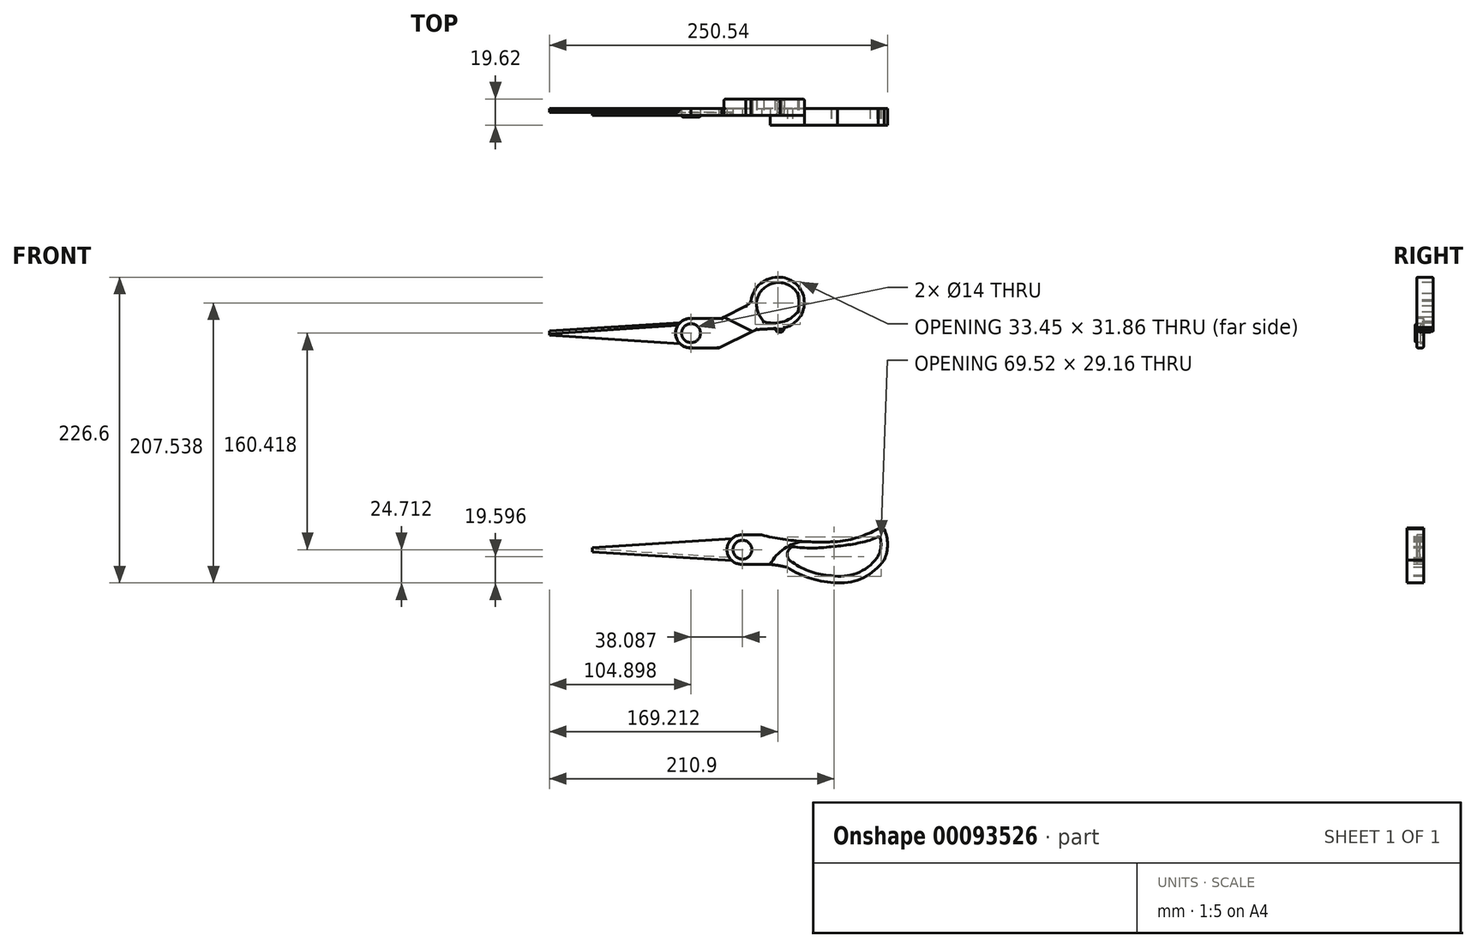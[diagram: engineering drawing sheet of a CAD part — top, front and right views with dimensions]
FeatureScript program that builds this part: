
annotation { "Feature Type Name" : "Feature", "Feature Type Description" : "" }
export const myFeature = defineFeature(function(context is Context, id is Id, definition is map)
    precondition{}
    {
        {
            var Q0;
            Q0=qCreatedBy(makeId("Front.planeOp"),FACE);
            var sketch = newSketch(context, id + "F0", { "sketchPlane" : qUnion([Q0])});
            skLineSegment(sketch, "E0", {"start": v(-93.78, 0) * mm, "end": v(95.08, 0) * mm, "construction": true});
            skLineSegment(sketch, "E1", {"start": v(-93.78, 0) * mm, "end": v(5.93, 0) * mm, "construction": true});
            skLineSegment(sketch, "E2", {"start": v(-93.78, 0) * mm, "end": v(-93.78, -1.57) * mm, "construction": true});
            skLineSegment(sketch, "E3", {"start": v(-93.78, 0) * mm, "end": v(-93.78, 1.57) * mm, "construction": true});
            skLineSegment(sketch, "E4", {"start": v(5.93, 0) * mm, "end": v(5.93, 8.05) * mm, "construction": true});
            skLineSegment(sketch, "E5", {"start": v(5.93, 0) * mm, "end": v(5.93, -8.05) * mm, "construction": true});
            skLineSegment(sketch, "E6", {"start": v(-93.78, 1.57) * mm, "end": v(5.93, 8.05) * mm});
            skLineSegment(sketch, "E7", {"start": v(-93.78, -1.57) * mm, "end": v(5.93, -8.05) * mm});
            skLineSegment(sketch, "E8", {"start": v(-93.78, 1.57) * mm, "end": v(-93.78, -1.57) * mm});
            skLineSegment(sketch, "E9", {"start": v(95.08, 0) * mm, "end": v(95.08, 32) * mm, "construction": true});
            skLineSegment(sketch, "E10", {"start": v(5.93, 0) * mm, "end": v(31.53, 0) * mm, "construction": true});
            skLineSegment(sketch, "E11", {"start": v(31.53, 0) * mm, "end": v(31.53, -10.87) * mm, "construction": true});
            skLineSegment(sketch, "E12", {"start": v(5.93, 0) * mm, "end": v(33.93, 0) * mm, "construction": true});
            skLineSegment(sketch, "E13", {"start": v(33.93, 0) * mm, "end": v(33.93, 10.87) * mm, "construction": true});
            skLineSegment(sketch, "E14", {"start": v(31.53, 0) * mm, "end": v(11.12, 0) * mm, "construction": true});
            skLineSegment(sketch, "E15", {"start": v(11.12, 0) * mm, "end": v(11.12, 10.87) * mm, "construction": true});
            skLineSegment(sketch, "E16", {"start": v(11.12, 0) * mm, "end": v(11.12, -10.87) * mm, "construction": true});
            skLineSegment(sketch, "E17", {"start": v(11.12, 0) * mm, "end": v(-0.31, 0) * mm, "construction": true});
            skArc(sketch, "E18", {"start": v(11.12, 10.87) * mm, "mid": v(-0.31, 0) * mm, "end": v(11.12, -10.87) * mm});
            skLineSegment(sketch, "E19", {"start": v(11.12, 10.87) * mm, "end": v(33.93, 10.87) * mm, "construction": true});
            skLineSegment(sketch, "E20", {"start": v(11.12, -10.87) * mm, "end": v(31.53, -10.87) * mm, "construction": true});
            skLineSegment(sketch, "E21", {"start": v(33.93, 0) * mm, "end": v(95.08, 32) * mm, "construction": true});
            skLineSegment(sketch, "E22", {"start": v(95.08, 32) * mm, "end": v(95.08, 50.8) * mm, "construction": true});
            skLineSegment(sketch, "E23", {"start": v(95.08, 32) * mm, "end": v(95.08, 13.2) * mm, "construction": true});
            skLineSegment(sketch, "E24", {"start": v(95.08, 32.55) * mm, "end": v(90.03, 29.91) * mm, "construction": true});
            skLineSegment(sketch, "E25", {"start": v(90.03, 29.36) * mm, "end": v(64.24, 15.86) * mm, "construction": true});
            skLineSegment(sketch, "E26", {"start": v(90.03, 29.91) * mm, "end": v(77.13, 23.16) * mm, "construction": true});
            skLineSegment(sketch, "E27", {"start": v(77.13, 22.6) * mm, "end": v(77.13, 3.81) * mm, "construction": true});
            skLineSegment(sketch, "E28", {"start": v(77.13, 22.6) * mm, "end": v(77.13, 41.41) * mm, "construction": true});
            skArc(sketch, "E29", {"start": v(77.13, 3.81) * mm, "mid": v(95.09, 22.61) * mm, "end": v(77.13, 41.41) * mm});
            skLineSegment(sketch, "E30", {"start": v(33.93, 0) * mm, "end": v(59.92, 13.6) * mm, "construction": true});
            skLineSegment(sketch, "E31", {"start": v(59.92, 13.6) * mm, "end": v(59.92, 24.47) * mm, "construction": true});
            skLineSegment(sketch, "E32", {"start": v(59.92, 13.6) * mm, "end": v(59.92, 2.73) * mm, "construction": true});
            skLineSegment(sketch, "E33", {"start": v(33.93, 10.87) * mm, "end": v(59.92, 24.47) * mm, "construction": true});
            skArc(sketch, "E34", {"start": v(77.13, 41.41) * mm, "mid": v(62.77, 36.88) * mm, "end": v(55.42, 23.74) * mm});
            skArc(sketch, "E35", {"start": v(51.68, 20.16) * mm, "mid": v(53.85, 21.63) * mm, "end": v(55.42, 23.74) * mm});
            skLineSegment(sketch, "E36", {"start": v(31.53, -10.87) * mm, "end": v(59.92, 2.73) * mm, "construction": true});
            skArc(sketch, "E37", {"start": v(59.92, 2.73) * mm, "mid": v(68.53, 3.17) * mm, "end": v(77.13, 3.81) * mm});
            skCircle(sketch, "E38", {"center": v(11.12, 0) * mm, "radius": 7 * mm});
            skLineSegment(sketch, "E39", {"start": v(95.08, 0.99) * mm, "end": v(73.17, 0.99) * mm, "construction": true});
            skLineSegment(sketch, "E40", {"start": v(73.17, 3.5) * mm, "end": v(73.17, 0.86) * mm});
            skLineSegment(sketch, "E41", {"start": v(73.17, 0.86) * mm, "end": v(80.38, 0.86) * mm});
            skLineSegment(sketch, "E42", {"start": v(80.38, 0.86) * mm, "end": v(80.38, 4.25) * mm});
            skLineSegment(sketch, "E43", {"start": v(77.5, 3.83) * mm, "end": v(77.5, 9.53) * mm, "construction": true});
            skLineSegment(sketch, "E44", {"start": v(95.08, 21.98) * mm, "end": v(86.61, 21.98) * mm, "construction": true});
            skLineSegment(sketch, "E45", {"start": v(65.06, 2.97) * mm, "end": v(65.06, 8.67) * mm});
            skLineSegment(sketch, "E46", {"start": v(90.15, 9.9) * mm, "end": v(90.15, 15.6) * mm, "construction": true});
            skArc(sketch, "E47", {"start": v(90.03, 29.36) * mm, "mid": v(73.3, 37.3) * mm, "end": v(59.92, 24.47) * mm});
            skArc(sketch, "E48", {"start": v(90.15, 15.6) * mm, "mid": v(91.16, 22.49) * mm, "end": v(90.03, 29.36) * mm});
            skArc(sketch, "E49", {"start": v(59.92, 24.47) * mm, "mid": v(60.59, 15.95) * mm, "end": v(65.06, 8.67) * mm});
            skArc(sketch, "E50", {"start": v(65.06, 8.67) * mm, "mid": v(78.66, 8.31) * mm, "end": v(90.15, 15.6) * mm});
            skLineSegment(sketch, "E51", {"start": v(11.12, 10.87) * mm, "end": v(33.93, 10.87) * mm});
            skLineSegment(sketch, "E52", {"start": v(33.93, 10.87) * mm, "end": v(51.68, 20.16) * mm});
            skLineSegment(sketch, "E53", {"start": v(11.12, -10.87) * mm, "end": v(31.53, -10.87) * mm});
            skLineSegment(sketch, "E54", {"start": v(31.53, -10.87) * mm, "end": v(59.92, 2.73) * mm});
            skLineSegment(sketch, "E55", {"start": v(31.53, -10.87) * mm, "end": v(54.22, 0) * mm, "construction": true});
            skLineSegment(sketch, "E56", {"start": v(31.53, -10.87) * mm, "end": v(50.38, -1.84) * mm, "construction": true});
            skLineSegment(sketch, "E57", {"start": v(56.83, 1.25) * mm, "end": v(35.63, 11.76) * mm});
            skSolve(sketch);
        }
        {
            var Q0;
            {var subQ0=sQuery(id+"F0.wireOp",EDGE,"E8");Q0=makeQuery(id+"F0.imprint","IMPRINT",FACE,{"disambiguationData":[TD([[makeQuery(id+"F0.imprint","IMPRINT",EDGE,{"derivedFrom":subQ0}),1.0]])]});}
            extrude(context, id + "F1", {"entities" : qUnion([Q0]), "oppositeDirection" : true, "depth" : 5.1 * mm, "hasSecondDirection" : true, "secondDirectionOppositeDirection" : true, "secondDirectionDepth" : 2.53 * mm});
        }
        {
            var Q0;
            Q0=makeQuery(id+"F0.imprint","IMPRINT",FACE,{"disambiguationData":[TD([[makeQuery(id+"F0.imprint","IMPRINT",EDGE,{"derivedFrom":sQuery(id+"F0.wireOp",EDGE,"E38")}),-1.0]])]});
            extrude(context, id + "F2", {"entities" : qUnion([Q0]), "oppositeDirection" : true, "depth" : 5.1 * mm});
        }
        {
            var Q0;
            {var subQ9=sQuery(id+"F0.wireOp",EDGE,"E34");Q0=makeQuery(id+"F0.imprint","IMPRINT",FACE,{"disambiguationData":[TD([[makeQuery(id+"F0.imprint","IMPRINT",EDGE,{"derivedFrom":subQ9}),1.0]])]});}
            var Q1;
            {var subQ0=sQuery(id+"F0.wireOp",EDGE,"E40");Q1=makeQuery(id+"F0.imprint","IMPRINT",FACE,{"disambiguationData":[TD([[makeQuery(id+"F0.imprint","IMPRINT",EDGE,{"derivedFrom":subQ0}),1.0]])]});}
            extrude(context, id + "F3", {"entities" : qUnion([Q0, Q1]), "oppositeDirection" : true, "depth" : 12.33 * mm});
        }
        {
            var Q0;
            Q0=makeQuery(id+"F3.opExtrude","CAP_EDGE",EDGE,{"disambiguationData":[OSD([sQuery(id+"F0.wireOp",EDGE,"E29")])],"isStart":false});
            var Q1;
            Q1=makeQuery(id+"F3.opExtrude","CAP_EDGE",EDGE,{"disambiguationData":[OSD([sQuery(id+"F0.wireOp",EDGE,"E34")])],"isStart":false});
            var Q2;
            Q2=makeQuery(id+"F3.opExtrude","CAP_EDGE",EDGE,{"disambiguationData":[OSD([sQuery(id+"F0.wireOp",EDGE,"E35")])],"isStart":false});
            var Q3;
            Q3=makeQuery(id+"F3.opExtrude","CAP_EDGE",EDGE,{"disambiguationData":[OSD([sQuery(id+"F0.wireOp",EDGE,"E52")])],"isStart":false});
            var Q4;
            Q4=makeQuery(id+"F3.opExtrude","CAP_EDGE",EDGE,{"disambiguationData":[OSD([sQuery(id+"F0.wireOp",EDGE,"E37")])],"isStart":false});
            var Q5;
            Q5=makeQuery(id+"F3.opExtrude","CAP_EDGE",EDGE,{"disambiguationData":[OSD([sQuery(id+"F0.wireOp",EDGE,"E54")])],"isStart":false});
            var Q6;
            Q6=makeQuery(id+"F3.opExtrude","CAP_EDGE",EDGE,{"disambiguationData":[OSD([sQuery(id+"F0.wireOp",EDGE,"E34")])],"isStart":true});
            var Q7;
            Q7=makeQuery(id+"F3.opExtrude","CAP_EDGE",EDGE,{"disambiguationData":[OSD([sQuery(id+"F0.wireOp",EDGE,"E35")])],"isStart":true});
            var Q8;
            {var subQ0=sQuery(id+"F0.wireOp",EDGE,"E52");Q8=makeQuery(id+"F3.boolean.opBoolean","MERGE",EDGE,{"derivedFrom":[makeQuery(id+"F2.opExtrude","CAP_EDGE",EDGE,{"disambiguationData":[OSD([subQ0])],"isStart":true}),makeQuery(id+"F3.opExtrude","CAP_EDGE",EDGE,{"disambiguationData":[OSD([subQ0])],"isStart":true})]});}
            var Q9;
            Q9=makeQuery(id+"F3.opExtrude","CAP_EDGE",EDGE,{"disambiguationData":[OSD([sQuery(id+"F0.wireOp",EDGE,"E29")])],"isStart":true});
            var Q10;
            Q10=makeQuery(id+"F3.opExtrude","CAP_EDGE",EDGE,{"disambiguationData":[OSD([sQuery(id+"F0.wireOp",EDGE,"E37")])],"isStart":true});
            var Q11;
            {var subQ0=sQuery(id+"F0.wireOp",EDGE,"E54");Q11=makeQuery(id+"F3.boolean.opBoolean","MERGE",EDGE,{"derivedFrom":[makeQuery(id+"F2.opExtrude","CAP_EDGE",EDGE,{"disambiguationData":[OSD([subQ0])],"isStart":true}),makeQuery(id+"F3.opExtrude","CAP_EDGE",EDGE,{"disambiguationData":[OSD([subQ0])],"isStart":true})]});}
            var Q12;
            Q12=makeQuery(id+"F2.opExtrude","CAP_EDGE",EDGE,{"disambiguationData":[OSD([sQuery(id+"F0.wireOp",EDGE,"E53")])],"isStart":true});
            var Q13;
            Q13=makeQuery(id+"F2.opExtrude","CAP_EDGE",EDGE,{"disambiguationData":[OSD([sQuery(id+"F0.wireOp",EDGE,"E18")])],"isStart":true});
            var Q14;
            Q14=makeQuery(id+"F2.opExtrude","CAP_EDGE",EDGE,{"disambiguationData":[OSD([sQuery(id+"F0.wireOp",EDGE,"E51")])],"isStart":true});
            var Q15;
            Q15=makeQuery(id+"F2.opExtrude","CAP_EDGE",EDGE,{"disambiguationData":[OSD([sQuery(id+"F0.wireOp",EDGE,"E51")])],"isStart":false});
            var Q16;
            Q16=makeQuery(id+"F2.opExtrude","CAP_EDGE",EDGE,{"disambiguationData":[OSD([sQuery(id+"F0.wireOp",EDGE,"E18")])],"isStart":false});
            var Q17;
            Q17=makeQuery(id+"F2.opExtrude","CAP_EDGE",EDGE,{"disambiguationData":[OSD([sQuery(id+"F0.wireOp",EDGE,"E53")])],"isStart":false});
            var Q18;
            Q18=makeQuery(id+"F2.opExtrude","CAP_EDGE",EDGE,{"disambiguationData":[OSD([sQuery(id+"F0.wireOp",EDGE,"E54")])],"isStart":false});
            var Q19;
            Q19=makeQuery(id+"F2.opExtrude","CAP_EDGE",EDGE,{"disambiguationData":[OSD([sQuery(id+"F0.wireOp",EDGE,"E52")])],"isStart":false});
            fillet(context, id + "F4", {"entities" : qUnion([Q0, Q1, Q2, Q3, Q4, Q5, Q6, Q7, Q8, Q9, Q10, Q11, Q12, Q13, Q14, Q15, Q16, Q17, Q18, Q19]), "radius" : 1 * mm, "tangentPropagation" : true, "allowEdgeOverflow" : false});
        }
        {
            var Q0;
            Q0=makeQuery(id+"F3.opExtrude","CAP_EDGE",EDGE,{"disambiguationData":[OSD([sQuery(id+"F0.wireOp",EDGE,"E50")])],"isStart":false});
            var Q1;
            Q1=makeQuery(id+"F3.opExtrude","CAP_EDGE",EDGE,{"disambiguationData":[OSD([sQuery(id+"F0.wireOp",EDGE,"E48")])],"isStart":false});
            var Q2;
            Q2=makeQuery(id+"F3.opExtrude","CAP_EDGE",EDGE,{"disambiguationData":[OSD([sQuery(id+"F0.wireOp",EDGE,"E47")])],"isStart":false});
            var Q3;
            Q3=makeQuery(id+"F3.opExtrude","CAP_EDGE",EDGE,{"disambiguationData":[OSD([sQuery(id+"F0.wireOp",EDGE,"E49")])],"isStart":false});
            fillet(context, id + "F5", {"entities" : qUnion([Q0, Q1, Q2, Q3]), "radius" : 1 * mm, "tangentPropagation" : true, "allowEdgeOverflow" : false});
        }
        {
            var Q0;
            Q0=makeQuery(id+"F3.opExtrude","CAP_EDGE",EDGE,{"disambiguationData":[OSD([sQuery(id+"F0.wireOp",EDGE,"E41")])],"isStart":false});
            var Q1;
            Q1=makeQuery(id+"F3.opExtrude","CAP_EDGE",EDGE,{"disambiguationData":[OSD([sQuery(id+"F0.wireOp",EDGE,"E41")])],"isStart":true});
            chamfer(context, id + "F6", {"entities" : qUnion([Q0, Q1]), "width" : 2 * mm, "tangentPropagation" : true});
        }
        {
            var Q0;
            Q0=makeQuery(id+"F3.opExtrude","SWEPT_EDGE",EDGE,{"disambiguationData":[OSD([sQuery(id+"F0.wireOp",EDGE,"E41"),sQuery(id+"F0.wireOp",EDGE,"E42")])]});
            var Q1;
            Q1=makeQuery(id+"F3.opExtrude","SWEPT_EDGE",EDGE,{"disambiguationData":[OSD([sQuery(id+"F0.wireOp",EDGE,"E40"),sQuery(id+"F0.wireOp",EDGE,"E41")])]});
            chamfer(context, id + "F7", {"entities" : qUnion([Q0, Q1]), "width" : 2 * mm, "tangentPropagation" : true});
        }
        {
            var Q0;
            Q0=qCreatedBy(makeId("Front.planeOp"),FACE);
            var sketch = newSketch(context, id + "F8", { "sketchPlane" : qUnion([Q0])});
            skLineSegment(sketch, "E58", {"start": v(-61.94, -160.42) * mm, "end": v(154.1, -160.42) * mm, "construction": true});
            skLineSegment(sketch, "E59", {"start": v(154.1, -160.42) * mm, "end": v(154.1, -145.1) * mm, "construction": true});
            skLineSegment(sketch, "E60", {"start": v(-61.94, -160.42) * mm, "end": v(-61.94, -158.85) * mm, "construction": true});
            skLineSegment(sketch, "E61", {"start": v(-61.94, -160.42) * mm, "end": v(-61.94, -161.98) * mm, "construction": true});
            skLineSegment(sketch, "E62", {"start": v(-61.94, -160.42) * mm, "end": v(37.77, -160.42) * mm, "construction": true});
            skLineSegment(sketch, "E63", {"start": v(37.77, -160.42) * mm, "end": v(37.77, -168.28) * mm, "construction": true});
            skLineSegment(sketch, "E64", {"start": v(37.77, -168.28) * mm, "end": v(39.02, -168.28) * mm, "construction": true});
            skLineSegment(sketch, "E65", {"start": v(37.77, -160.42) * mm, "end": v(37.77, -152.56) * mm, "construction": true});
            skLineSegment(sketch, "E66", {"start": v(37.77, -152.56) * mm, "end": v(39.02, -152.56) * mm, "construction": true});
            skLineSegment(sketch, "E67", {"start": v(-61.94, -158.85) * mm, "end": v(37.77, -152.56) * mm, "construction": true});
            skLineSegment(sketch, "E68", {"start": v(-61.94, -161.98) * mm, "end": v(37.77, -168.28) * mm, "construction": true});
            skLineSegment(sketch, "E69", {"start": v(37.77, -160.42) * mm, "end": v(49.2, -160.42) * mm, "construction": true});
            skLineSegment(sketch, "E70", {"start": v(37.77, -160.42) * mm, "end": v(63.37, -160.42) * mm, "construction": true});
            skLineSegment(sketch, "E71", {"start": v(37.77, -160.42) * mm, "end": v(65.77, -160.42) * mm, "construction": true});
            skLineSegment(sketch, "E72", {"start": v(65.77, -160.42) * mm, "end": v(65.77, -149.55) * mm, "construction": true});
            skLineSegment(sketch, "E73", {"start": v(63.37, -160.42) * mm, "end": v(63.37, -171.29) * mm, "construction": true});
            skLineSegment(sketch, "E74", {"start": v(49.2, -160.42) * mm, "end": v(49.2, -149.55) * mm, "construction": true});
            skLineSegment(sketch, "E75", {"start": v(49.2, -160.42) * mm, "end": v(49.2, -171.29) * mm, "construction": true});
            skArc(sketch, "E76", {"start": v(49.2, -149.55) * mm, "mid": v(37.77, -160.42) * mm, "end": v(49.2, -171.29) * mm});
            skLineSegment(sketch, "E77", {"start": v(154.1, -160.42) * mm, "end": v(154.1, -175.73) * mm, "construction": true});
            skLineSegment(sketch, "E78", {"start": v(65.77, -160.42) * mm, "end": v(154.1, -175.73) * mm, "construction": true});
            skLineSegment(sketch, "E79", {"start": v(119.62, -169.76) * mm, "end": v(119.62, -185.07) * mm, "construction": true});
            skLineSegment(sketch, "E80", {"start": v(119.62, -169.76) * mm, "end": v(119.62, -154.44) * mm, "construction": true});
            skLineSegment(sketch, "E81", {"start": v(154.1, -175.73) * mm, "end": v(143.62, -173.92) * mm, "construction": true});
            skLineSegment(sketch, "E82", {"start": v(143.62, -173.92) * mm, "end": v(114.98, -168.95) * mm, "construction": true});
            skLineSegment(sketch, "E83", {"start": v(114.98, -168.95) * mm, "end": v(114.98, -158.25) * mm, "construction": true});
            skLineSegment(sketch, "E84", {"start": v(114.98, -168.95) * mm, "end": v(114.98, -179.65) * mm, "construction": true});
            skLineSegment(sketch, "E85", {"start": v(63.37, -160.42) * mm, "end": v(63.37, -149.55) * mm, "construction": true});
            skLineSegment(sketch, "E86", {"start": v(49.2, -149.55) * mm, "end": v(63.37, -149.55) * mm});
            skLineSegment(sketch, "E87", {"start": v(65.77, -160.42) * mm, "end": v(65.77, -171.29) * mm, "construction": true});
            skLineSegment(sketch, "E88", {"start": v(49.2, -171.29) * mm, "end": v(65.77, -171.29) * mm});
            skLineSegment(sketch, "E89", {"start": v(82.4, -163.3) * mm, "end": v(82.4, -153.04) * mm, "construction": true});
            skLineSegment(sketch, "E90", {"start": v(82.4, -163.3) * mm, "end": v(82.4, -173.56) * mm, "construction": true});
            skArc(sketch, "E91", {"start": v(82.4, -173.56) * mm, "mid": v(74.16, -171.86) * mm, "end": v(65.77, -171.29) * mm});
            skLineSegment(sketch, "E92", {"start": v(143.62, -173.92) * mm, "end": v(86.34, -163.98) * mm, "construction": true});
            skLineSegment(sketch, "E93", {"start": v(86.34, -163.98) * mm, "end": v(86.34, -158.22) * mm, "construction": true});
            skLineSegment(sketch, "E94", {"start": v(86.34, -163.98) * mm, "end": v(86.34, -169.74) * mm, "construction": true});
            skArc(sketch, "E95", {"start": v(82.4, -173.56) * mm, "mid": v(100.24, -181.8) * mm, "end": v(119.62, -185.07) * mm});
            skArc(sketch, "E96", {"start": v(119.62, -185.07) * mm, "mid": v(139.1, -181.1) * mm, "end": v(154.1, -168.08) * mm});
            skArc(sketch, "E97", {"start": v(63.37, -149.55) * mm, "mid": v(91.32, -154.07) * mm, "end": v(119.62, -154.44) * mm});
            skLineSegment(sketch, "E98", {"start": v(149.65, -160.42) * mm, "end": v(149.65, -145.1) * mm, "construction": true});
            skArc(sketch, "E99", {"start": v(119.62, -154.44) * mm, "mid": v(135.09, -151.22) * mm, "end": v(149.65, -145.1) * mm});
            skArc(sketch, "E100", {"start": v(154.1, -145.1) * mm, "mid": v(151.88, -144.4) * mm, "end": v(149.65, -145.1) * mm});
            skArc(sketch, "E101", {"start": v(154.1, -168.08) * mm, "mid": v(156.76, -156.59) * mm, "end": v(154.1, -145.1) * mm});
            skLineSegment(sketch, "E102", {"start": v(82.4, -163.3) * mm, "end": v(152.27, -170.55) * mm, "construction": true});
            skLineSegment(sketch, "E103", {"start": v(143.62, -169.65) * mm, "end": v(143.62, -157.37) * mm, "construction": true});
            skLineSegment(sketch, "E104", {"start": v(137.13, -160.42) * mm, "end": v(137.13, -155.84) * mm, "construction": true});
            skArc(sketch, "E105", {"start": v(86.34, -169.74) * mm, "mid": v(99.94, -176.8) * mm, "end": v(115.03, -179.54) * mm});
            skArc(sketch, "E106", {"start": v(86.34, -158.22) * mm, "mid": v(100.66, -159.2) * mm, "end": v(114.98, -158.25) * mm});
            skArc(sketch, "E107", {"start": v(86.34, -158.22) * mm, "mid": v(82.36, -163.98) * mm, "end": v(86.34, -169.74) * mm});
            skLineSegment(sketch, "E108", {"start": v(143.62, -157.37) * mm, "end": v(143.62, -153.44) * mm, "construction": true});
            skArc(sketch, "E109", {"start": v(114.98, -158.25) * mm, "mid": v(129.42, -156.59) * mm, "end": v(143.62, -153.44) * mm});
            skLineSegment(sketch, "E110", {"start": v(149.65, -160.42) * mm, "end": v(149.65, -151.02) * mm, "construction": true});
            skArc(sketch, "E111", {"start": v(149.65, -151.02) * mm, "mid": v(146.62, -152.19) * mm, "end": v(143.62, -153.44) * mm, "construction": true});
            skLineSegment(sketch, "E112", {"start": v(151.44, -160.42) * mm, "end": v(151.44, -152.3) * mm, "construction": true});
            skArc(sketch, "E113", {"start": v(151.44, -152.3) * mm, "mid": v(150.87, -151.2) * mm, "end": v(149.65, -151.02) * mm, "construction": true});
            skLineSegment(sketch, "E114", {"start": v(148.9, -160.42) * mm, "end": v(148.9, -166.52) * mm, "construction": true});
            skArc(sketch, "E115", {"start": v(115.03, -179.54) * mm, "mid": v(133.83, -177.88) * mm, "end": v(148.9, -166.52) * mm});
            skArc(sketch, "E116", {"start": v(151.44, -152.3) * mm, "mid": v(150.87, -151.2) * mm, "end": v(149.65, -151.02) * mm});
            skArc(sketch, "E117", {"start": v(148.9, -166.52) * mm, "mid": v(151.6, -159.67) * mm, "end": v(151.44, -152.3) * mm});
            skLineSegment(sketch, "E118", {"start": v(-61.94, -158.85) * mm, "end": v(41.37, -152.33) * mm});
            skLineSegment(sketch, "E119", {"start": v(-61.94, -161.98) * mm, "end": v(-55.88, -162.37) * mm});
            skLineSegment(sketch, "E120", {"start": v(-61.94, -161.98) * mm, "end": v(41.37, -168.5) * mm});
            skLineSegment(sketch, "E121", {"start": v(-61.94, -158.85) * mm, "end": v(-61.94, -161.98) * mm});
            skArc(sketch, "E122", {"start": v(95.14, -154.36) * mm, "mid": v(80.28, -159.6) * mm, "end": v(69.88, -171.43) * mm});
            skCircle(sketch, "E123", {"center": v(49.2, -160.42) * mm, "radius": 7 * mm});
            skArc(sketch, "E124", {"start": v(149.65, -151.02) * mm, "mid": v(146.62, -152.19) * mm, "end": v(143.62, -153.44) * mm});
            skSolve(sketch);
        }
        {
            var Q0;
            Q0=makeQuery(id+"F3.opExtrude","CAP_EDGE",EDGE,{"disambiguationData":[OSD([sQuery(id+"F0.wireOp",EDGE,"E47")])],"isStart":true});
            var Q1;
            Q1=makeQuery(id+"F3.opExtrude","CAP_EDGE",EDGE,{"disambiguationData":[OSD([sQuery(id+"F0.wireOp",EDGE,"E48")])],"isStart":true});
            var Q2;
            Q2=makeQuery(id+"F3.opExtrude","CAP_EDGE",EDGE,{"disambiguationData":[OSD([sQuery(id+"F0.wireOp",EDGE,"E50")])],"isStart":true});
            var Q3;
            Q3=makeQuery(id+"F3.opExtrude","CAP_EDGE",EDGE,{"disambiguationData":[OSD([sQuery(id+"F0.wireOp",EDGE,"E49")])],"isStart":true});
            fillet(context, id + "F9", {"entities" : qUnion([Q0, Q1, Q2, Q3]), "radius" : 1 * mm, "tangentPropagation" : true, "allowEdgeOverflow" : false});
        }
        {
            var Q0;
            Q0=makeQuery(id+"F0.imprint","IMPRINT",FACE,{"disambiguationData":[TD([[makeQuery(id+"F0.imprint","IMPRINT",EDGE,{"derivedFrom":sQuery(id+"F0.wireOp",EDGE,"E38")}),1.0]])]});
            var Q1;
            Q1=sQuery(id+"F0.wireOp",EDGE,"E38");
            extrude(context, id + "F10", {"entities" : qUnion([Q0]), "surfaceEntities" : qUnion([Q1]), "depth" : 1 * mm});
        }
        {
            var Q0;
            Q0=makeQuery(id+"F10.opExtrude","CAP_EDGE",EDGE,{"disambiguationData":[OSD([sQuery(id+"F0.wireOp",EDGE,"E38")])],"isStart":false});
            fillet(context, id + "F11", {"entities" : qUnion([Q0]), "radius" : 1 * mm, "tangentPropagation" : true, "allowEdgeOverflow" : false});
        }
        {
            var Q0;
            {var subQ0=sQuery(id+"F8.wireOp",EDGE,"E118");Q0=makeQuery(id+"F8.imprint","IMPRINT",FACE,{"disambiguationData":[TD([[makeQuery(id+"F8.imprint","IMPRINT",EDGE,{"derivedFrom":subQ0}),-1.0]])]});}
            extrude(context, id + "F12", {"entities" : qUnion([Q0]), "oppositeDirection" : true, "depth" : 2.43 * mm});
        }
        {
            var Q0;
            {var subQ0=sQuery(id+"F8.wireOp",EDGE,"E86");Q0=makeQuery(id+"F8.imprint","IMPRINT",FACE,{"disambiguationData":[TD([[makeQuery(id+"F8.imprint","IMPRINT",EDGE,{"derivedFrom":subQ0}),-1.0]])]});}
            extrude(context, id + "F13", {"entities" : qUnion([Q0]), "oppositeDirection" : true, "depth" : 5.13 * mm});
        }
        {
            var Q0;
            {var subQ3=sQuery(id+"F8.wireOp",EDGE,"E95");Q0=makeQuery(id+"F8.imprint","IMPRINT",FACE,{"disambiguationData":[TD([[makeQuery(id+"F8.imprint","IMPRINT",EDGE,{"derivedFrom":subQ3}),1.0]])]});}
            extrude(context, id + "F14", {"entities" : qUnion([Q0]), "oppositeDirection" : true, "depth" : 5.13 * mm, "hasSecondDirection" : true, "secondDirectionOppositeDirection" : false, "secondDirectionDepth" : 7.3 * mm});
        }
        {
            var Q0;
            Q0=makeQuery(id+"F1.opExtrude","CAP_EDGE",EDGE,{"disambiguationData":[OSD([sQuery(id+"F0.wireOp",EDGE,"E6")])],"isStart":true});
            chamfer(context, id + "F15", {"entities" : qUnion([Q0]), "width" : 2 * mm, "tangentPropagation" : true});
        }
        {
            var Q0;
            Q0=makeQuery(id+"F12.opExtrude","CAP_EDGE",EDGE,{"disambiguationData":[OSD([sQuery(id+"F8.wireOp",EDGE,"E120")])],"isStart":false});
            chamfer(context, id + "F16", {"entities" : qUnion([Q0]), "width" : 2 * mm, "tangentPropagation" : true});
        }
    });
